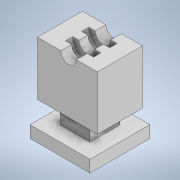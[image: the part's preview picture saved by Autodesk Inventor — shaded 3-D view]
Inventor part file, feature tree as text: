
AUTODESK INVENTOR PART (.ipt)
format: ipt  version: 2021 (Build 250183000, 183)  size: 205,312 bytes
history: native  units: in
note: dims shown in document units (in); Inventor stores cm internally (conversion verified against a paired STEP export)
features: sketch x12, extrude x11
ambient origin geometry x8: Origin, YZ Plane, XZ Plane, XY Plane, X Axis, Y Axis, Z Axis, Center Point
bodies: Solid2 (feature_tree)
feature tree (23):
  extrude  "Extrusion1"  Depth=2.9528in
  extrude  "Extrusion2"  Depth=0.1969in
  sketch  "Sketch3"  dims[d5=0.1969in d6=0.1969in]
  extrude  "Extrusion14"  Depth=0.1969in
  extrude  "Extrusion15"  Depth=2.3228in TaperAngle=0.0deg
  extrude  "Extrusion16"  Depth=2.3622in
  extrude  "Extrusion17"  Depth=0.9843in TaperAngle=0.0deg
  extrude  "Extrusion18"  Depth=0.4764in TaperAngle=0.0deg
  extrude  "Extrusion19"  Depth=0.9843in TaperAngle=0.0deg
  extrude  "Extrusion21"  Depth=0.4764in TaperAngle=0.0deg
  sketch  "Sketch20"  dims[d56=2.3228in d57=0.0in d58=2.9528in d59=0.0in]
  extrude  "Extrusion22"  Depth=2.9528in TaperAngle=0.0deg
  extrude  "Extrusion23"  Depth=0.4921in
  sketch  "Sketch1"  dims[d0=3.937in d1=2.9528in]
  sketch  "Sketch2"  dims[d2=2.3622in d3=0.0in d4=0.1969in]
  sketch  "Sketch13"  dims[d7=0.1969in d8=2.3228in d9=0.0in]
  sketch  "Sketch14"  dims[d10=1.0236in d11=2.3622in]
  sketch  "Sketch15"  dims[d44=0.9843in d45=2.3228in d46=0.0in]
  sketch  "Sketch16"  dims[d47=1.8508in d48=0.4764in d49=0.0in]
  sketch  "Sketch17"  dims[d50=0.9843in d51=2.3228in d52=0.0in]
  sketch  "Sketch19"  dims[d53=1.8508in d54=0.4764in d55=0.0in]
  sketch  "Sketch21"  dims[d64=1.1811in d65=0.0in d66=0.4921in]
  sketch  "Sketch22"  dims[d67=0.4921in d68=0.9843in d69=0.9843in d70=1.1811in d71=0.0in d72=0.9843in d73=0.9843in d74=0.9843in d75=0.9843in d76=0.7874in d77=0.0in d78=0.0197in d79=0.0344in]
